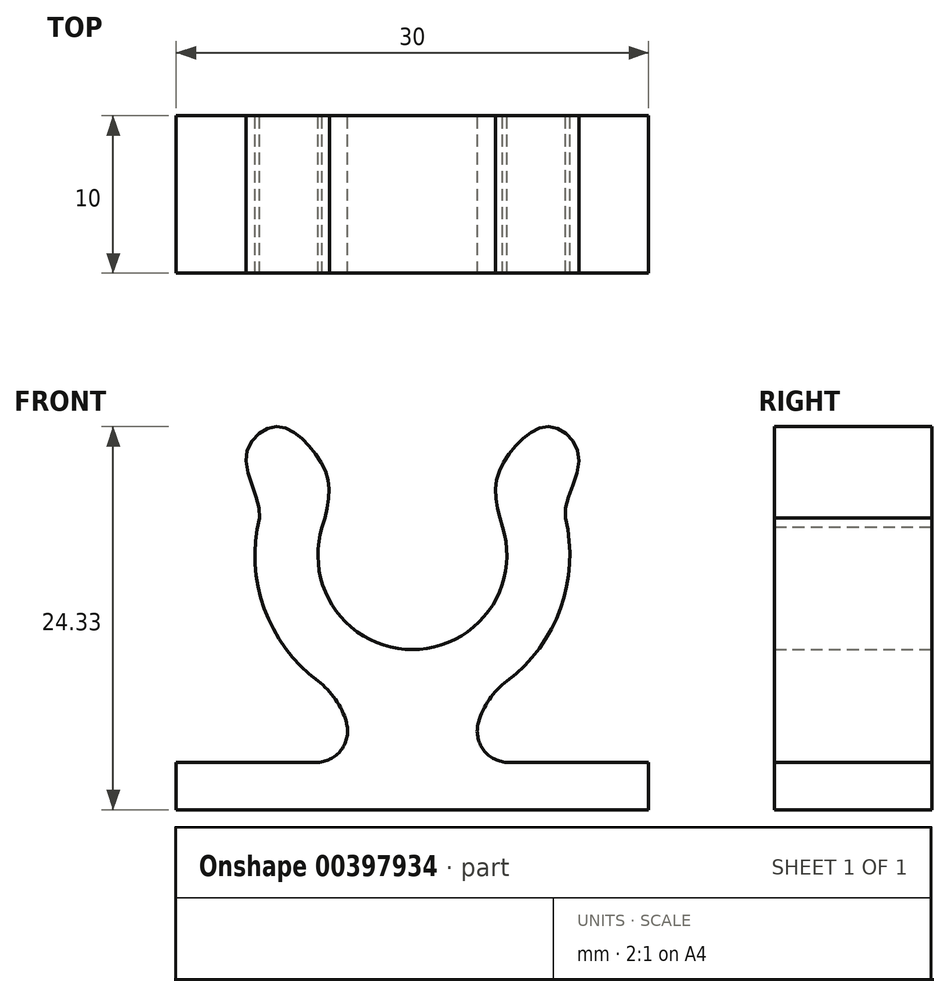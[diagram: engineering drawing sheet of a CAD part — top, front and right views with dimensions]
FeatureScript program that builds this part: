
annotation { "Feature Type Name" : "Feature", "Feature Type Description" : "" }
export const myFeature = defineFeature(function(context is Context, id is Id, definition is map)
    precondition{}
    {
        {
            var Q0;
            Q0=qCreatedBy(makeId("Front.planeOp"),FACE);
            var sketch = newSketch(context, id + "F0", { "sketchPlane" : qUnion([Q0])});
            skArc(sketch, "E0", {"start": v(-5.73, 1.8) * mm, "mid": v(0, -6) * mm, "end": v(5.73, 1.8) * mm});
            skArc(sketch, "E1", {"start": v(-9.72, 2.35) * mm, "mid": v(-9.41, -3.38) * mm, "end": v(-6, -8) * mm});
            skLineSegment(sketch, "E2.right", {"start": v(4, -12) * mm, "end": v(4, -13.17) * mm});
            skCircle(sketch, "E3", {"center": v(0, 0) * mm, "radius": 8 * mm, "construction": true});
            skLineSegment(sketch, "E4", {"start": v(-12.31, 0) * mm, "end": v(13.78, 0) * mm, "construction": true});
            skLineSegment(sketch, "E5", {"start": v(0, 11.63) * mm, "end": v(0, -20.94) * mm, "construction": true});
            skFitSpline(sketch, "E6", {"points": [v(-5.73, 1.8) * mm, v(-5.3, 4.46) * mm, v(-6.5, 6.86) * mm, v(-8.77, 8.16) * mm, v(-10.57, 6.26) * mm, v(-9.72, 2.35) * mm], "startDerivative": vector(3.67, 13.01) * mm, "endDerivative": vector(-2.28, -13.72) * mm});
            skFitSpline(sketch, "E7.MirrorCS", {"points": [v(5.73, 1.8) * mm, v(5.3, 4.46) * mm, v(6.5, 6.86) * mm, v(8.77, 8.16) * mm, v(10.57, 6.26) * mm, v(9.72, 2.35) * mm], "startDerivative": vector(-3.67, 13.01) * mm, "endDerivative": vector(2.28, -13.72) * mm});
            skArc(sketch, "E8.trimOffspring", {"start": v(6, -8) * mm, "mid": v(9.41, -3.38) * mm, "end": v(9.72, 2.35) * mm});
            skPoint(sketch, "E9.visualSharp", {"position": v(-4, -9.17) * mm});
            skArc(sketch, "E9.filletArc", {"start": v(-4.2, -10.6) * mm, "mid": v(-4.89, -9.16) * mm, "end": v(-6, -8) * mm});
            skPoint(sketch, "E10.visualSharp", {"position": v(4, -9.17) * mm});
            skArc(sketch, "E10.filletArc", {"start": v(6, -8) * mm, "mid": v(4.89, -9.16) * mm, "end": v(4.2, -10.6) * mm});
            skLineSegment(sketch, "E11.bottom", {"start": v(-15, -13.17) * mm, "end": v(-6.12, -13.17) * mm});
            skLineSegment(sketch, "E11.top", {"start": v(-15, -16.17) * mm, "end": v(15, -16.17) * mm});
            skLineSegment(sketch, "E11.left", {"start": v(-15, -13.17) * mm, "end": v(-15, -16.17) * mm});
            skLineSegment(sketch, "E11.right", {"start": v(15, -13.17) * mm, "end": v(15, -16.17) * mm});
            skLineSegment(sketch, "E12.trimOffspring", {"start": v(6.12, -13.17) * mm, "end": v(15, -13.17) * mm});
            skArc(sketch, "E13.filletArc", {"start": v(-6.12, -13.17) * mm, "mid": v(-4.52, -12.37) * mm, "end": v(-4.2, -10.6) * mm});
            skArc(sketch, "E14.filletArc", {"start": v(4.2, -10.6) * mm, "mid": v(4.52, -12.37) * mm, "end": v(6.12, -13.17) * mm});
            skSolve(sketch);
        }
        {
            var Q0;
            Q0 = qSketchRegion(id + "F0", true);
            extrude(context, id + "F1", {"entities" : qUnion([Q0]), "endBound" : BoundingType.SYMMETRIC, "depth" : 10 * mm});
        }
    });
